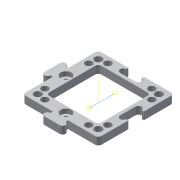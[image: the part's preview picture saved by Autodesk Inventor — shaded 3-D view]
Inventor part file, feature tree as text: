
AUTODESK INVENTOR PART (.ipt)
format: ipt  version: 2022 (Build 260153000, 153)  size: 350,208 bytes
history: native  units: mm
features: sketch x4, extrude x3, projected_geometry x3, mirror x2, other x1, pattern_circular x1, hole x1
ambient origin geometry x8: Origin, YZ Plane, XZ Plane, XY Plane, X Axis, Y Axis, Z Axis, Center Point
bodies: Volumenkörper1 (feature_tree)
feature tree (15):
  extrude  "Extrusion1"  TaperAngle=0.0deg  [1 undecoded]
  mirror  "Mirror6"
  mirror  "Mirror7"
  extrude  "Extrusion13"  TaperAngle=0.0deg  [1 undecoded]
  extrude  "Extrusion14"  TaperAngle=0.0deg  [1 undecoded]
  other  "Work Axis4"
  pattern_circular  "Circular Pattern6"  [2 undecoded]
  hole  "Hole7"  [1 undecoded]
  sketch  "Skizze1"  dims[d5=0.0mm d6=0.0mm]
  sketch  "Sketch26"  dims[d7=0.0mm d8=0.0mm]
  projected_geometry  "Projected Loop21"
  sketch  "Sketch28"  dims[d9=0.0mm d13=0.0mm]
  sketch  "Sketch29"  dims[d14=0.0mm d20=0.0mm d21=0.0mm d22=0.0mm d23=0.0mm d24=0.0mm d25=3.0mm d26=0.0mm d27=0.0mm d28=0.0mm d29=0.0mm d30=0.0mm d31=0.0mm d32=0.0mm d33=0.0mm d34=0.0mm d46=0.0mm d47=0.0mm d48=0.0mm d49=-10.0mm d50=0.0mm d51=0.0mm d52=0.0mm d53=0.0mm d54=0.0mm d55=0.0mm d56=0.0mm d57=0.0mm d58=0.0mm d59=0.0mm d77=2.65mm d82=2.65mm d222=0.5mm d236=5.3mm d278=25.0mm d279=25.0mm d2=7.75mm d281=7.75mm d282=2.0mm d283=4.9mm d284=20.0mm d4=20.0mm d286=4.6mm d290=20.8mm d292=2.0mm d293=5.5mm d294=14.0mm d296=10.0mm d297=1.5mm d298=10.0mm d299=0.0mm d300=1.95mm d301=0.5mm d302=10.0mm d303=0.0mm d308=20.0mm d309=90.0deg d313=6.3mm d314=6.3mm d319=7.78mm d320=4.11mm d322=4.11mm d323=3.2mm d324=6.0mm d325=7.0mm d326=3.0mm d327=90.0deg d328=8.0mm d329=20.594885mm d330=0.0mm d331=0.0mm d332=0.0mm d357=5.0mm d358=5.5mm d359=0.1mm]
  projected_geometry  "Projected Loop24"
  projected_geometry  "Projizierte Kontur27"
note: 6 required parameter values undecoded (feature->parameter linkage not recoverable at this tier; creation-order binding heuristic only, values carry confidence <= 0.55)
